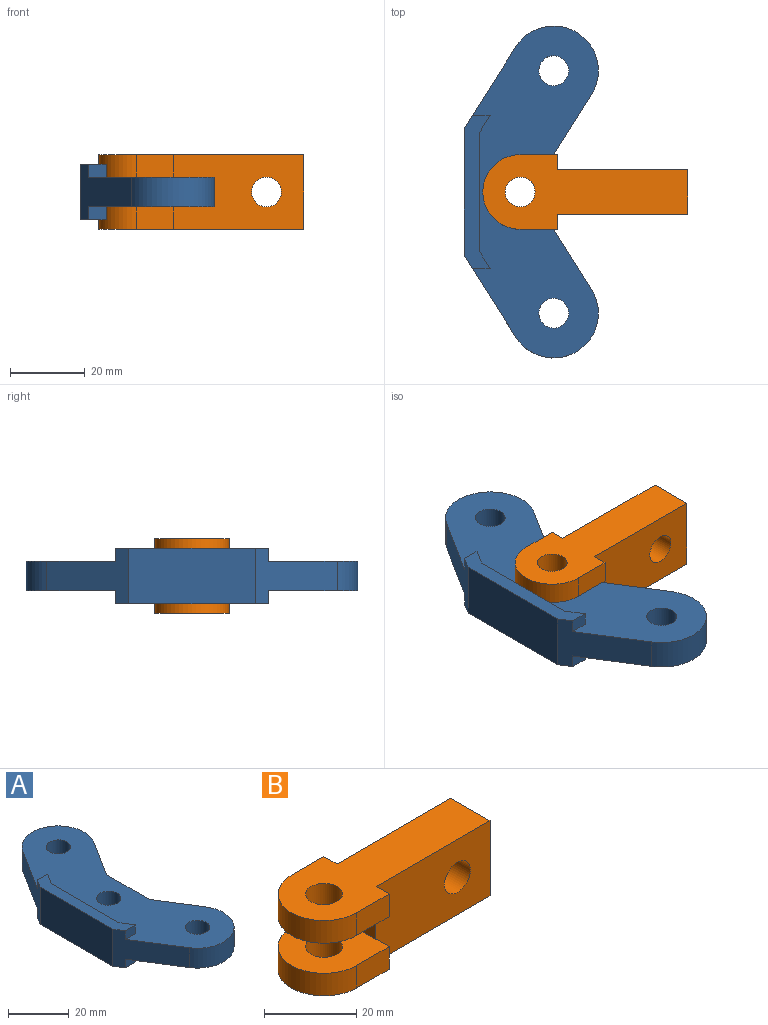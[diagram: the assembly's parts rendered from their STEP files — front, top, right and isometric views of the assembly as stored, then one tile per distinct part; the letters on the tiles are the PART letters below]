
ASSEMBLY  parts=2 mates=1
PART A: 25 faces, bbox 36x89x15 mm
  f0: plane 21.97x15mm, normal (-0.85,-0.53,0), area 237.2mm2, adj f1,f10,f11,f13,f17,f18,f23,f24
  f1: cylinder r=12mm len=22.15mm, axis (0,0,-1), area 301.6mm2, adj f0,f2,f10,f11
  f2: plane 16.1x10.15mm, normal (0.85,0.53,0), area 152.3mm2, adj f1,f3,f10,f11
  f3: plane 20x8mm, normal (1,0,0), area 160mm2, adj f2,f4,f10,f11
  f4: plane 16.1x10.15mm, normal (0.85,-0.53,0), area 152.3mm2, adj f3,f5,f10,f11
  f5: cylinder r=12mm len=22.15mm, axis (0,0,-1), area 301.6mm2, adj f4,f6,f10,f11
  f6: plane 21.97x15mm, normal (-0.85,0.53,0), area 237.2mm2, adj f5,f10,f11,f16,f17,f22,f23,f24
  f7: cylinder r=4mm len=8mm, axis (0,0,-1), area 201.1mm2, adj f10,f11
  f8: cylinder r=4mm len=8mm, axis (0,0,-1), area 201.1mm2, adj f10,f11
  f9: cylinder r=4mm len=8mm, axis (0,0,-1), area 201.1mm2, adj f10,f11
  f10: plane 89x33.75mm, normal (0,0,1), area 1858mm2, adj f0,f1,f2,f3,f4,f5,f6,f7
  f11: plane 89x33.75mm, normal (0,0,-1), area 1858mm2, adj f0,f1,f2,f3,f4,f5,f6,f7
  f12: plane 31.56x3.5mm, normal (1,0,0), area 110.4mm2, adj f10,f19,f21,f23
  f13: plane 4.73x3.5mm, normal (0,-1,0), area 16.6mm2, adj f0,f11,f14,f24
  f14: plane 4.72x3.5mm, normal (0.85,0.53,0), area 19.5mm2, adj f11,f13,f20,f24
  f15: plane 4.72x3.5mm, normal (0.85,-0.53,0), area 19.5mm2, adj f11,f16,f20,f24
  f16: plane 4.73x3.5mm, normal (0,1,0), area 16.6mm2, adj f6,f11,f15,f24
  f17: plane 33.87x15mm, normal (-1,0,0), area 508mm2, adj f0,f6,f23,f24
  f18: plane 4.73x3.5mm, normal (0,-1,0), area 16.6mm2, adj f0,f10,f19,f23
  f19: plane 4.72x3.5mm, normal (0.85,0.53,0), area 19.5mm2, adj f10,f12,f18,f23
  f20: plane 31.56x3.5mm, normal (1,0,0), area 110.4mm2, adj f11,f14,f15,f24
  f21: plane 4.72x3.5mm, normal (0.85,-0.53,0), area 19.5mm2, adj f10,f12,f22,f23
  f22: plane 4.73x3.5mm, normal (0,1,0), area 16.6mm2, adj f6,f10,f21,f23
  f23: plane 41x6.98mm, normal (0,0,1), area 170mm2, adj f0,f6,f12,f17,f18,f19,f21,f22
  f24: plane 41x6.98mm, normal (0,0,-1), area 170mm2, adj f0,f6,f13,f14,f15,f16,f17,f20
PART B: 21 faces, bbox 55x20x20 mm
  f0: plane 35x20mm, normal (0,-1,0), area 649.3mm2, adj f2,f4,f9,f10,f11,f12,f13,f18
  f1: plane 35x20mm, normal (0,1,0), area 649.3mm2, adj f2,f3,f9,f10,f11,f12,f13,f14
  f2: plane 12x8mm, normal (-1,0,0), area 96mm2, adj f0,f1,f9,f20
  f3: plane 6x4mm, normal (1,0,0), area 24mm2, adj f1,f5,f9,f10
  f4: plane 6x4mm, normal (1,0,0), area 24mm2, adj f0,f8,f9,f10
  f5: plane 10x6mm, normal (0,1,0), area 60mm2, adj f3,f6,f9,f10
  f6: cylinder r=10mm len=20mm, axis (0,0,-1), area 188.5mm2, adj f5,f8,f9,f10
  f7: cylinder r=4mm len=8mm, axis (0,0,-1), area 150.8mm2, adj f9,f10
  f8: plane 10x6mm, normal (0,-1,0), area 60mm2, adj f4,f6,f9,f10
  f9: plane 20x20mm, normal (0,0,1), area 306.4mm2, adj f0,f1,f2,f3,f4,f5,f6,f7
  f10: plane 54.97x20mm, normal (0,0,-1), area 726.4mm2, adj f0,f1,f3,f4,f5,f6,f7,f8
  f11: plane 20x12mm, normal (1,0,0), area 240mm2, adj f0,f1,f10,f12
  f12: plane 54.97x20mm, normal (0,0,1), area 726.4mm2, adj f0,f1,f11,f14,f15,f16,f17,f18
  f13: cylinder r=4mm len=12mm, axis (0,1,0), area 301.6mm2, adj f0,f1
  f14: plane 6x4mm, normal (1,0,0), area 24mm2, adj f1,f12,f15,f20
  f15: plane 10x6mm, normal (0,1,0), area 60mm2, adj f12,f14,f16,f20
  f16: cylinder r=10mm len=20mm, axis (0,0,-1), area 188.5mm2, adj f12,f15,f17,f20
  f17: plane 10x6mm, normal (0,-1,0), area 60mm2, adj f12,f16,f18,f20
  f18: plane 6x4mm, normal (1,0,0), area 24mm2, adj f0,f12,f17,f20
  f19: cylinder r=4mm len=8mm, axis (0,0,-1), area 150.8mm2, adj f12,f20
  f20: plane 20x20mm, normal (0,0,-1), area 306.4mm2, adj f0,f1,f2,f14,f15,f16,f17,f18
PLACE A t=(65.63,0.08,9.26)mm
PLACE B t=(-3.37,0.08,-0.74)mm
MATE revolute A.f7 <-> B.f6  axis (0,0,-1) through (6.67,0.08,13.26)mm
